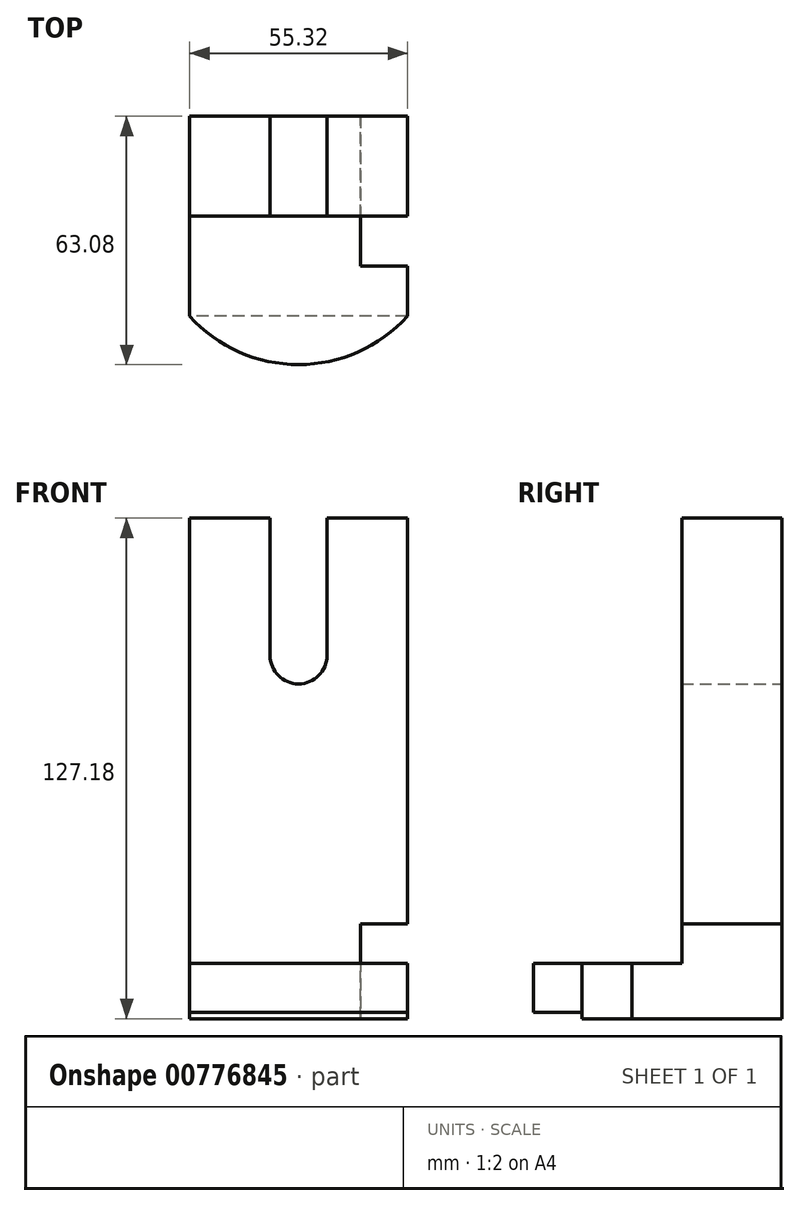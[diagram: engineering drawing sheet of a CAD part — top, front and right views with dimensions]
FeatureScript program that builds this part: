
annotation { "Feature Type Name" : "Feature", "Feature Type Description" : "" }
export const myFeature = defineFeature(function(context is Context, id is Id, definition is map)
    precondition{}
    {
        {
            var Q0;
            Q0=qCreatedBy(makeId("Front.planeOp"),FACE);
            var sketch = newSketch(context, id + "F0", { "sketchPlane" : qUnion([Q0])});
            skLineSegment(sketch, "E0.bottom", {"start": v(27.66, 63.6) * mm, "end": v(-27.66, 63.6) * mm});
            skLineSegment(sketch, "E0.top", {"start": v(27.66, -63.6) * mm, "end": v(-27.66, -63.6) * mm});
            skLineSegment(sketch, "E0.left", {"start": v(27.66, 63.6) * mm, "end": v(27.66, -63.6) * mm});
            skLineSegment(sketch, "E0.right", {"start": v(-27.66, 63.6) * mm, "end": v(-27.66, -63.6) * mm});
            skPoint(sketch, "E0.middle", {"position": v(0, 0) * mm});
            skSolve(sketch);
        }
        {
            var Q0;
            Q0 = qSketchRegion(id + "F0", true);
            extrude(context, id + "F1", {"entities" : qUnion([Q0]), "oppositeDirection" : true, "depth" : 25.4 * mm, "offsetDistance" : 25.4 * mm});
        }
        {
            var Q0;
            Q0=makeQuery(id+"F1.opExtrude","CAP_FACE",FACE,{"disambiguationData":[OSD([sQuery(id+"F0.wireOp",EDGE,"E0.bottom"),sQuery(id+"F0.wireOp",EDGE,"E0.top"),sQuery(id+"F0.wireOp",EDGE,"E0.left"),sQuery(id+"F0.wireOp",EDGE,"E0.right")])],"isStart":true});
            var sketch = newSketch(context, id + "F2", { "sketchPlane" : qUnion([Q0])});
            skLineSegment(sketch, "E1.bottom", {"start": v(0, 63.6) * mm, "end": v(-7.23, 63.6) * mm});
            skLineSegment(sketch, "E1.top", {"start": v(0, 28.7) * mm, "end": v(-7.23, 28.7) * mm});
            skLineSegment(sketch, "E1.left", {"start": v(0, 63.6) * mm, "end": v(0, 28.7) * mm});
            skLineSegment(sketch, "E1.right", {"start": v(-7.23, 63.6) * mm, "end": v(-7.23, 28.7) * mm});
            skLineSegment(sketch, "E2.bottom", {"start": v(0, 28.7) * mm, "end": v(7.23, 28.7) * mm});
            skLineSegment(sketch, "E2.top", {"start": v(0, 63.6) * mm, "end": v(7.23, 63.6) * mm});
            skLineSegment(sketch, "E2.left", {"start": v(0, 28.7) * mm, "end": v(0, 63.6) * mm});
            skLineSegment(sketch, "E2.right", {"start": v(7.23, 28.7) * mm, "end": v(7.23, 63.6) * mm});
            skSolve(sketch);
        }
        {
            var Q0;
            Q0=makeQuery(id+"F2.imprint","IMPRINT",FACE,{"disambiguationData":[TD([[makeQuery(id+"F2.imprint","IMPRINT",EDGE,{"derivedFrom":sQuery(id+"F2.wireOp",EDGE,"E1.bottom")}),1.0]])]});
            var Q1;
            Q1=makeQuery(id+"F2.imprint","IMPRINT",FACE,{"disambiguationData":[TD([[makeQuery(id+"F2.imprint","IMPRINT",EDGE,{"derivedFrom":sQuery(id+"F2.wireOp",EDGE,"E2.bottom")}),1.0]])]});
            extrude(context, id + "F3", {"entities" : qUnion([Q0, Q1]), "operationType" : NewBodyOperationType.REMOVE, "oppositeDirection" : true, "depth" : 25.4 * mm, "offsetDistance" : 25.4 * mm});
        }
        {
            var Q0;
            Q0=makeQuery(id+"F1.opExtrude","CAP_FACE",FACE,{"disambiguationData":[OSD([sQuery(id+"F0.wireOp",EDGE,"E0.bottom"),sQuery(id+"F0.wireOp",EDGE,"E0.top"),sQuery(id+"F0.wireOp",EDGE,"E0.left"),sQuery(id+"F0.wireOp",EDGE,"E0.right")])],"isStart":false});
            var sketch = newSketch(context, id + "F4", { "sketchPlane" : qUnion([Q0])});
            skArc(sketch, "E3", {"start": v(-7.23, 28.7) * mm, "mid": v(0, 21.47) * mm, "end": v(7.23, 28.7) * mm});
            skSolve(sketch);
        }
        {
            var Q0;
            Q0 = qSketchRegion(id + "F4", true);
            var Q1;
            Q1=makeQuery(id+"F4.imprint","IMPRINT",FACE,{"disambiguationData":[TD([[makeQuery(id+"F4.imprint","IMPRINT",EDGE,{"derivedFrom":sQuery(id+"F4.wireOp",EDGE,"E3")}),1.0]])]});
            extrude(context, id + "F5", {"entities" : qUnion([Q0, Q1]), "operationType" : NewBodyOperationType.REMOVE, "oppositeDirection" : true, "depth" : 25.4 * mm, "offsetDistance" : 25.4 * mm});
        }
        {
            var Q0;
            Q0=makeQuery(id+"F1.opExtrude","CAP_FACE",FACE,{"disambiguationData":[OSD([sQuery(id+"F0.wireOp",EDGE,"E0.bottom"),sQuery(id+"F0.wireOp",EDGE,"E0.top"),sQuery(id+"F0.wireOp",EDGE,"E0.left"),sQuery(id+"F0.wireOp",EDGE,"E0.right")])],"isStart":true});
            var sketch = newSketch(context, id + "F6", { "sketchPlane" : qUnion([Q0])});
            skLineSegment(sketch, "E4.bottom", {"start": v(-27.66, -63.6) * mm, "end": v(27.66, -63.6) * mm});
            skLineSegment(sketch, "E4.top", {"start": v(-27.66, -49.55) * mm, "end": v(27.66, -49.55) * mm});
            skLineSegment(sketch, "E4.left", {"start": v(-27.66, -63.6) * mm, "end": v(-27.66, -49.55) * mm});
            skLineSegment(sketch, "E4.right", {"start": v(27.66, -63.6) * mm, "end": v(27.66, -49.55) * mm});
            skSolve(sketch);
        }
        {
            var Q0;
            Q0 = qSketchRegion(id + "F6", true);
            extrude(context, id + "F7", {"entities" : qUnion([Q0]), "operationType" : NewBodyOperationType.ADD, "depth" : 25.4 * mm, "offsetDistance" : 25.4 * mm});
        }
        {
            var Q0;
            Q0=makeQuery(id+"F7.opExtrude","SWEPT_FACE",FACE,{"disambiguationData":[OSD([sQuery(id+"F6.wireOp",EDGE,"E4.top")])]});
            var sketch = newSketch(context, id + "F8", { "sketchPlane" : qUnion([Q0])});
            skArc(sketch, "E5", {"start": v(-27.66, -25.4) * mm, "mid": v(0, -37.68) * mm, "end": v(27.66, -25.4) * mm});
            skSolve(sketch);
        }
        {
            var Q0;
            Q0=makeQuery(id+"F8.imprint","IMPRINT",FACE,{"disambiguationData":[TD([[makeQuery(id+"F8.imprint","IMPRINT",EDGE,{"derivedFrom":sQuery(id+"F8.wireOp",EDGE,"E5")}),1.0]])]});
            extrude(context, id + "F9", {"entities" : qUnion([Q0]), "operationType" : NewBodyOperationType.ADD, "oppositeDirection" : true, "depth" : 12.45 * mm, "offsetDistance" : 25.4 * mm});
        }
        {
            var Q0;
            Q0=makeQuery(id+"F7.boolean.opBoolean","MERGE",FACE,{"derivedFrom":[makeQuery(id+"F1.opExtrude","SWEPT_FACE",FACE,{"disambiguationData":[OSD([sQuery(id+"F0.wireOp",EDGE,"E0.left")])]}),makeQuery(id+"F7.opExtrude","SWEPT_FACE",FACE,{"disambiguationData":[OSD([sQuery(id+"F6.wireOp",EDGE,"E4.right")])]})]});
            var sketch = newSketch(context, id + "F10", { "sketchPlane" : qUnion([Q0])});
            skLineSegment(sketch, "E6.bottom", {"start": v(0, -39.54) * mm, "end": v(25.4, -39.54) * mm});
            skLineSegment(sketch, "E6.top", {"start": v(0, -63.6) * mm, "end": v(25.4, -63.6) * mm});
            skLineSegment(sketch, "E6.left", {"start": v(0, -39.54) * mm, "end": v(0, -63.6) * mm});
            skLineSegment(sketch, "E6.right", {"start": v(25.4, -39.54) * mm, "end": v(25.4, -63.6) * mm});
            skSolve(sketch);
        }
        {
            var Q0;
            Q0 = qSketchRegion(id + "F10", true);
            extrude(context, id + "F11", {"entities" : qUnion([Q0]), "operationType" : NewBodyOperationType.REMOVE, "oppositeDirection" : true, "depth" : 11.94 * mm, "offsetDistance" : 25.4 * mm});
        }
        {
            var Q0;
            {var subQ0=sQuery(id+"F6.wireOp",EDGE,"E4.top");Q0=makeQuery(id+"F9.boolean.opBoolean","MERGE",FACE,{"derivedFrom":[makeQuery(id+"F7.opExtrude","SWEPT_FACE",FACE,{"disambiguationData":[OSD([subQ0])]}),makeQuery(id+"F9.opExtrude","CAP_FACE",FACE,{"disambiguationData":[OSD([subQ0,sQuery(id+"F8.wireOp",EDGE,"E5")])],"isStart":true})]});}
            var sketch = newSketch(context, id + "F12", { "sketchPlane" : qUnion([Q0])});
            skLineSegment(sketch, "E7.bottom", {"start": v(15.73, 0) * mm, "end": v(27.66, 0) * mm});
            skLineSegment(sketch, "E7.top", {"start": v(15.73, -12.7) * mm, "end": v(27.66, -12.7) * mm});
            skLineSegment(sketch, "E7.left", {"start": v(15.73, 0) * mm, "end": v(15.73, -12.7) * mm});
            skLineSegment(sketch, "E7.right", {"start": v(27.66, 0) * mm, "end": v(27.66, -12.7) * mm});
            skSolve(sketch);
        }
        {
            var Q0;
            Q0=makeQuery(id+"F12.imprint","IMPRINT",FACE,{"disambiguationData":[TD([[makeQuery(id+"F12.imprint","IMPRINT",EDGE,{"derivedFrom":sQuery(id+"F12.wireOp",EDGE,"E7.bottom")}),-1.0]])]});
            extrude(context, id + "F13", {"entities" : qUnion([Q0]), "operationType" : NewBodyOperationType.REMOVE, "oppositeDirection" : true, "depth" : 25.4 * mm, "offsetDistance" : 25.4 * mm});
        }
    });
